# Revit family: PRD_FrankeWS_WtrSpplFttngsFrWshBsnsAndTrghs_ElectronicBibTap_F3EV1004,1022
name_source: partatom
category: Plumbing Fixtures
revit_build: Autodesk Revit 2018 (Build: 20190510_1515(x64)
units: mm (PartAtom-declared; Revit-internal decimal feet)

## family parameters
Cut with Voids When Loaded = Yes
Host = Face
OmniClass Number = 23.45.55.14
OmniClass Title = Single Faucets
Part Type = Normal
Room Calculation Point = No
Round Connector Dimension = Use Diameter
Shared = No

## types (2) — shared parameters
AssetType = Fixed
Category = Pr_40_20_87_98, Washbasin taps
Color = Chrome
Default Elevation = 750 mm  [stored 2.46063 ft]
DefaultAutomaticHygieneFlushing = 24h after the last activity
Depressurised = no
DiameterNominal = 15.000 mm
DurationUnit = year
FaucetFunction = MIXED
FaucetOperation = ELECTRONIC
FaucetType = BIB
Features = For sanitary facilities. For connection to pre-mixed hot or cold water. High-polished chromium-plated brass.
Finish = high-polished chromium-plated brass
FlowColdWater = 0.1 L/s
FunctionalPrinciple = electronic self-closing
HygieneFlushing = yes
IfcExportAs = IfcValveType
IfcExportType = FAUCET
InletSize = G-1-2-B
Manufacturer = KWC Group AG
ManufacturerName = KWC Group AG
ManufacturerURL = www.kwc.com
Material = Brass
MaterialsBody = Brass
MinimumFlowPressure = 1.00 bar
NBSDescription = Water supply fittings for wash basins and troughs
NBSReference = 45-35-70/371
NominalLength = 210 mm  [stored 0.688976 ft]
NominalWidth = 50 mm  [stored 0.164042 ft]
OutletMaterial = PRD_AR_SyntheticGrey
PowerConsumption = 1.5
PowerSupplyConnection = Battery 6 V
ProductInformation = https://pim.kwc.com
ProtectiveShutdown = yes
ProtectiveSystemIP = IP59K
SensorMaterial = PRD_AR_SyntheticDarkGrey
SoundInsulation = no
SpoutProjection = 130.00 mm
TapMaterial = PRD_AR_ChromatedBrass_HighPolished
ThermalDisinfection = automatic thermal disinfection installed
TypeOfMixing = no mixing
TypeOfMounting = Wall mounting
TypeOfOperation = sensor operation
TypeOfSensor = opto-electronic sensor
TypeOfTap = bib tap
URL = www.kwc.com
Uniclass2015Code = Pr_40_20_87_98
Uniclass2015Title = Washbasin taps
Uniclass2015Version = Products v1.10
Version = 1
WarrantyDurationUnit = year
zero-valued in all types: NominalHeight

## per-type parameters (varying)
| type | BIMObjectName | Description | GrossWeight | Model | ModelNumber | ModelReference | Name | NetWeight | VolumeFlowRate |
| F3EV1004 - 0.10 L/s | PRD_AR_WaterSupplyFittingsForWashBasinsAndTroughs_ElectronicBibTap_F3EV1004 | F3E bib tap DN 15 for wall mounting for sanitary facilities, opto-electronically controlled. For connection to pre-mixed hot or cold water. Control electronics, solenoid valve cartridge, 6 V lithium battery (CR-P2) and sensor in all-metal housing, high-polished chromium-plated brass. Aerator with integrated flow regulator 6.0 l/min. Activated water hygiene flushing 24 hours after last activation, safety switch-off with continuous reflection and saving of statistical data. With option for parameterization and communication via optional, bidirectional remote control. | 2.05 kg | F3EV1004 | 2030036177 | F3EV1004 | F3 electronic bib tap F3EV1004 | 1.93 kg | 0.10 L/s at 3 bar |
| F3EV1022 - 0.05 L/s | PRD_AR_WaterSupplyFittingsForWashBasinsAndTroughs_ElectronicBibTap_F3EV1022 | F3E bib tap DN 15 for wall mounting for sanitary facilities, opto-electronically controlled. For connection to pre-mixed hot or cold water. Control electronics, solenoid valve cartridge, 6 V lithium battery (CR-P2) and sensor in all-metal housing, high-polished chromium-plated brass. Aerator with integrated flow regulator 3.0 l/min. Activated water hygiene flushing 24 hours after last activation, safety switch-off with continuous reflection and saving of statistical data. With option for parameterization and communication via optional, bidirectional remote control. | 1.92 kg | F3EV1022 | 2030040224 | F3EV1022 | F3 electronic bib tap F3EV1022 | 1.82 kg | 0.05 L/s at 3 bar |

note: [stored X ft] marks values corroborated as IEEE doubles in the binary element streams (Revit-internal decimal feet)

## geometry (parser evidence)
native form markers: Sweep x1
no freeform markers — native parametric forms only
